# Revit family: CCSQ
name_source: partatom
category: Lighting Fixtures
units: mm (PartAtom-declared; Revit-internal decimal feet)

## family parameters
Cut with Voids When Loaded = No
Host = Face
Light Source = Yes
OmniClass Number = 23.80.70.11.21
OmniClass Title = Emergency Lighting
Part Type = Normal
Room Calculation Point = No
Round Connector Dimension = Use Diameter
Shared = No

## types (2) — shared parameters
Color Filter = 16777215
Default Elevation = 48.000"
Description = LED Combination Exit/Emergency Light
Dimming Lamp Color Temperature Shift = <None>
Emit Shape Visible in Rendering = No
Emit from Rectangle Length = 10.000"
Emit from Rectangle Width = 5.000"
Finish = White
Is 120VAC = Yes
Is 277VAC = No
Lamp = LED Lamp
Load Classification = Lighting
Manufacturer = Compass Products
Model = CC SQ
Photometric Web File = generic
Power Factor = 1
Tilt Angle = 0.00°
URL = https://www.currentlighting.com
Voltage = 120 V
Wattage Comments = High lumen output lamp-head run at 1.7 watts per lamp

## per-type parameters (varying)
| type | Apparent Load | Lamp Option | Lens | Watts |
| CCRHOSQ | 4 VA | Sq. Head : CCRHOSQ | Red Glass | 4 W |
| CCGHOSQ | 5 VA | Sq. Head : CCGHOSQ | Green Glass | 5 W |

## geometry (parser evidence)
native form markers: Blend x8, Sweep x6
no freeform markers — native parametric forms only
